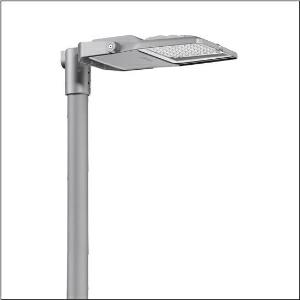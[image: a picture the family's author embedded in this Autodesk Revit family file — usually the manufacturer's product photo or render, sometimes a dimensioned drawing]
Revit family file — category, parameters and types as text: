
# Revit family: floodlight_fl_21_iq_mini___pl64_5xa7772d4e3a_9d14
name_source: partatom
category: Lighting Fixtures
units: mm (PartAtom-declared; Revit-internal decimal feet)

## family parameters
Cut with Voids When Loaded = No
Host = Face
Light Source = No
Part Type = Normal
Room Calculation Point = No
Round Connector Dimension = Use Diameter
Shared = No

## types (1)
- --- (1 x LED, 17970 lm, 143 W, 4000K)
    Apparent Load = 143 VA
    CIE Flux Codes = 28 80 98 100 100
    Color Rendering = 70
    Color Temperature = 4000K
    Default Elevation = 1800 mm
    Description = Floodlight FL 21 iQ mini, floodlight, primary light control with lens, of PMMA, primary optical cover: protective disc, of toughened safety glass, transparent, light distribution: PL64, light emission: direct distribution, installation type: surface-mounted, LED, High Power LED, rated luminous flux: 17.970lm, luminous efficacy: 126lm/W, light colour: 740, colour temperature: 4000K, control: Auto-Match, Temp-Guard, Night-Set, Smart-Wire, Desk-Remote (wireless, voltage-free reading and setting of iQ features in the workshop via application-optimized NFC function/RFID function), optimised constant luminous flux control (CLO 2.0), Light-Fading, Lumen-Switch, with terminal, 6-pole, mains connection: 220..240V, AC, 50/60Hz, start of lifetime: 143W, end of service life: 152W, reduction: 61W, luminaire housing, of diecast aluminium, powder-coated, Siteco® metallic grey (DB 702S), corrosivity category C5 mid according to DIN EN ISO 12944, sealing non-destructively replaceable, please order mast flange separately, mast bracket, of steel, galvanised, powder-coated, protection rating (complete): IP66, insulation class (complete): insulation class II (safety insulation), certification: CE, ENEC, VDE, protection symbol: D, impact resistance: IK08, permissible operating ambient temperature: -40..+40°C, permissible operating ambient temperature for outdoor applications: -40..+50°C, standard: DIN EN 12944, LABS conformity tested according to VDMA 24364:2018-05, packaging unit: 1 piece

Light Distribution: PL64
    Height = 70 mm
    Lamp = 1 x LED
    Lamp Light Flux = 17970 lm
    Lamp Power = 143 W
    Lamp count = 1
    Length = 485 mm
    Luminous efficacy = 126 lm/W
    Manufacturer = Siteco
    ModVariant = No
    Model = 5XA7772D4E3A
    Number of Poles = 1
    OnlyDefault = Yes
    Power Factor = 1
    Product Name = Floodlight FL 21 iQ mini | PL64
    Product group = floodlight | pylon annexe
    ProductGroupID = 6200
    Protection Class = Protection class II
    Protection Degree = IP 66
    RLX_Detail_Level = 1
    RLX_Emergency_Light_Flux = 0 lm
    RLX_Emergency_Type = 0
    RLX_Emergency_Type_DB = No
    RlxData = <blob elided: 101553 chars, md5=de05d0db>
    Socket = socket
    Standby Power = 0 W
    System Light Flux = 17970 lm
    System Power = 143 W
    Type Comments = factory setting: luminous flux: 100 % | dim-lin: 254 | 730 mA
    Type Image = l_1007125.jpg
    URL = http://relux.com
    VarID = @adj_115801
    Voltage = 0 V
    Weight = 0.00 kg
    Width = 337 mm

## geometry (parser evidence)
native form markers: Blend x4, Sweep x12
no freeform markers — native parametric forms only
